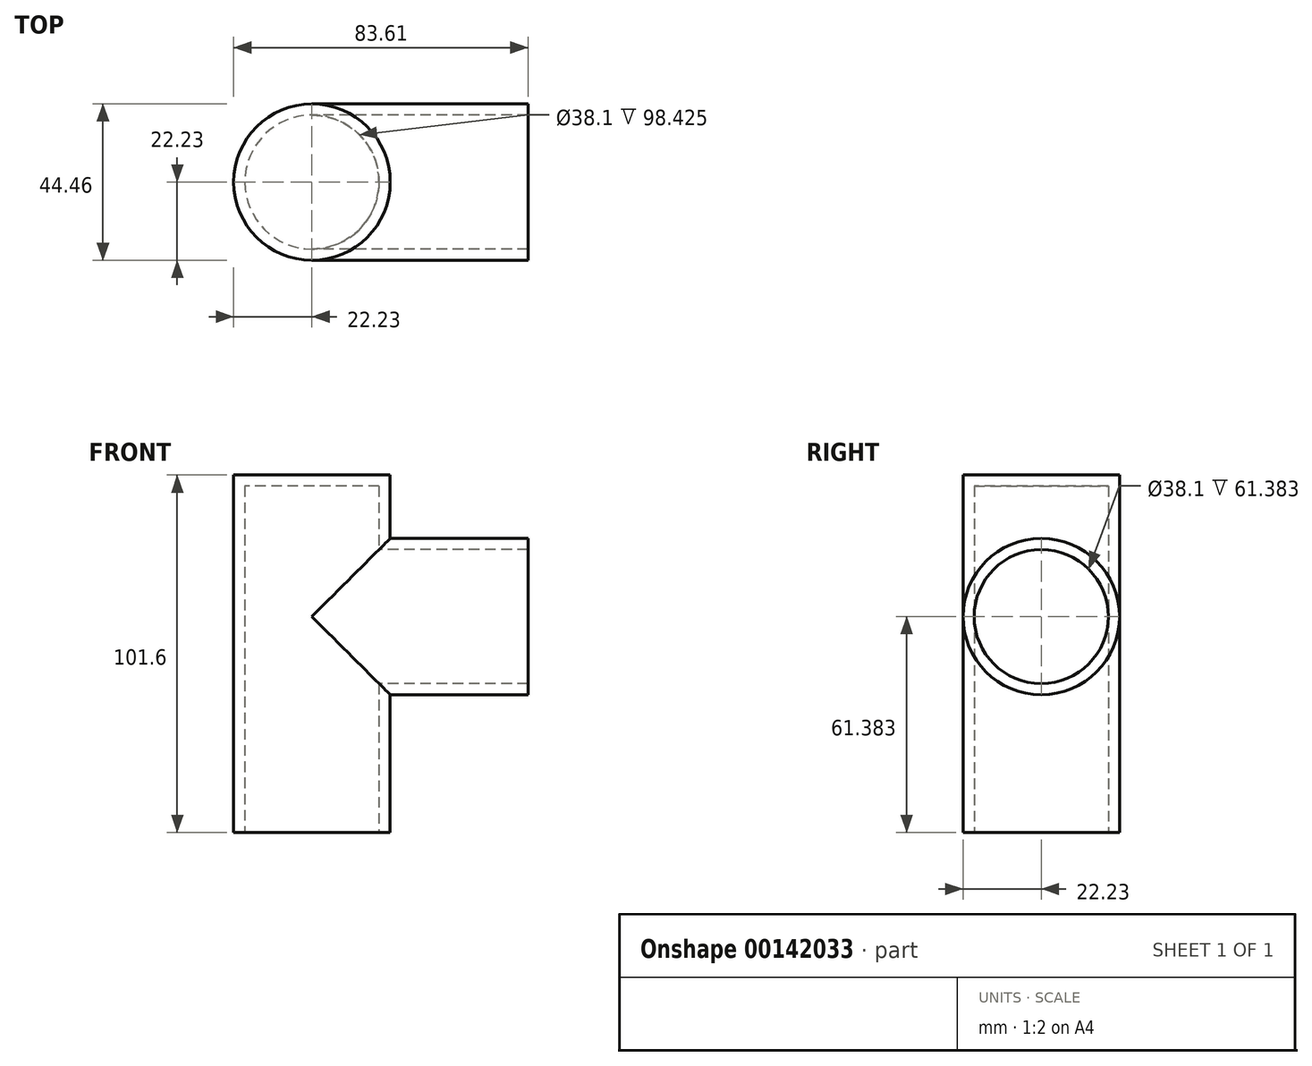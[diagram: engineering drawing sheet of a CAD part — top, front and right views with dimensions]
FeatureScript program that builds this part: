
annotation { "Feature Type Name" : "Feature", "Feature Type Description" : "" }
export const myFeature = defineFeature(function(context is Context, id is Id, definition is map)
    precondition{}
    {
        {
            var Q0;
            Q0=qCreatedBy(makeId("Top.planeOp"),FACE);
            var sketch = newSketch(context, id + "F0", { "sketchPlane" : qUnion([Q0])});
            skCircle(sketch, "E0", {"center": v(0, 0) * mm, "radius": 19.05 * mm});
            skCircle(sketch, "E1", {"center": v(0, 0) * mm, "radius": 22.23 * mm});
            skSolve(sketch);
        }
        {
            var Q0;
            Q0 = qSketchRegion(id + "F0", true);
            extrude(context, id + "F1", {"entities" : qUnion([Q0]), "depth" : 76.2 * mm});
        }
        {
            var Q0;
            Q0=makeQuery(id+"F0.imprint","IMPRINT",FACE,{"disambiguationData":[TD([[makeQuery(id+"F0.imprint","IMPRINT",EDGE,{"derivedFrom":sQuery(id+"F0.wireOp",EDGE,"E0")}),1.0]])]});
            var Q1;
            Q1=makeQuery(id+"F0.imprint","IMPRINT",FACE,{"disambiguationData":[TD([[makeQuery(id+"F0.imprint","IMPRINT",EDGE,{"derivedFrom":sQuery(id+"F0.wireOp",EDGE,"E0")}),-1.0]])]});
            extrude(context, id + "F2", {"entities" : qUnion([Q0, Q1]), "operationType" : NewBodyOperationType.ADD, "depth" : 76.2 * mm, "hasSecondDirection" : true, "secondDirectionOppositeDirection" : false, "secondDirectionDepth" : 73.02 * mm});
        }
        {
            var Q0;
            Q0=qCreatedBy(makeId("Right.planeOp"),FACE);
            var sketch = newSketch(context, id + "F3", { "sketchPlane" : qUnion([Q0])});
            skLineSegment(sketch, "E2", {"start": v(0, 0) * mm, "end": v(0, 35.98) * mm, "construction": true});
            skCircle(sketch, "E3", {"center": v(0, 35.98) * mm, "radius": 22.23 * mm});
            skCircle(sketch, "E4", {"center": v(0, 35.98) * mm, "radius": 19.05 * mm});
            skSolve(sketch);
        }
        {
            var Q0;
            Q0 = qSketchRegion(id + "F3", true);
            extrude(context, id + "F4", {"entities" : qUnion([Q0]), "operationType" : NewBodyOperationType.ADD, "depth" : 35.98 * mm});
        }
        {
            var Q0;
            Q0=makeQuery(id+"F0.imprint","IMPRINT",FACE,{"disambiguationData":[TD([[makeQuery(id+"F0.imprint","IMPRINT",EDGE,{"derivedFrom":sQuery(id+"F0.wireOp",EDGE,"E0")}),1.0]])]});
            extrude(context, id + "F5", {"entities" : qUnion([Q0]), "operationType" : NewBodyOperationType.REMOVE, "depth" : 63.5 * mm});
        }
        {
            var Q0;
            Q0=makeQuery(id+"F3.imprint","IMPRINT",FACE,{"disambiguationData":[TD([[makeQuery(id+"F3.imprint","IMPRINT",EDGE,{"derivedFrom":sQuery(id+"F3.wireOp",EDGE,"E4")}),1.0]])]});
            extrude(context, id + "F6", {"entities" : qUnion([Q0]), "operationType" : NewBodyOperationType.REMOVE, "depth" : 25.4 * mm});
        }
        {
            var Q0;
            Q0=makeQuery(id+"F4.opExtrude","CAP_FACE",FACE,{"disambiguationData":[OSD([sQuery(id+"F3.wireOp",EDGE,"E3"),sQuery(id+"F3.wireOp",EDGE,"E4")])],"isStart":false});
            extrude(context, id + "F7", {"entities" : qUnion([Q0]), "operationType" : NewBodyOperationType.ADD, "depth" : 25.4 * mm});
        }
        {
            var Q0;
            Q0=makeQuery(id+"F1.opExtrude","CAP_FACE",FACE,{"disambiguationData":[OSD([sQuery(id+"F0.wireOp",EDGE,"E0"),sQuery(id+"F0.wireOp",EDGE,"E1")])],"isStart":true});
            extrude(context, id + "F8", {"entities" : qUnion([Q0]), "operationType" : NewBodyOperationType.ADD, "depth" : 25.4 * mm});
        }
    });
